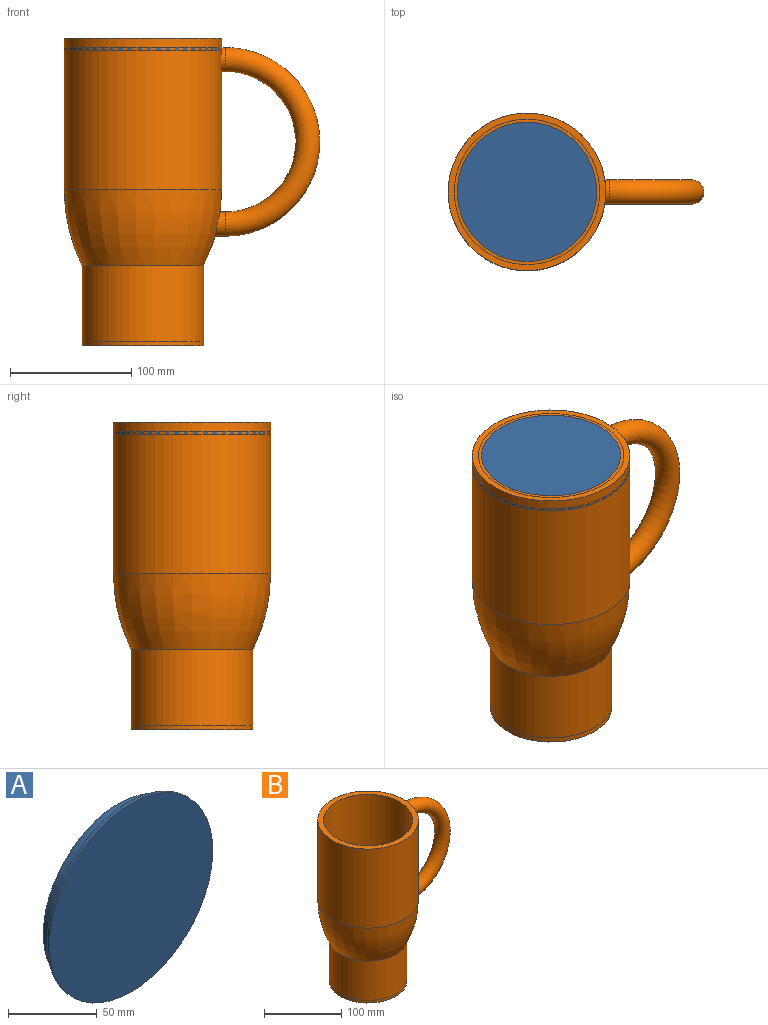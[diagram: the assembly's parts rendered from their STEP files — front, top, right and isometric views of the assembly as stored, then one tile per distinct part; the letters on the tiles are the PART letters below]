
ASSEMBLY  parts=2 mates=1
PART A: 5 faces, bbox 130x10x130 mm
  f0: cylinder r=60mm len=120mm, axis (0,-1,0), area 3015.9mm2, adj f1,f3
  f1: plane 120x120mm, normal (0,1,0), area 11309.7mm2, adj f0
  f2: cylinder r=65mm len=130mm, axis (0,-1,0), area 816.8mm2, adj f3,f4
  f3: plane 130x130mm, normal (0,1,0), area 1963.5mm2, adj f0,f2
  f4: plane 130x130mm, normal (0,-1,0), area 13273.2mm2, adj f2
PART B: 12 faces, bbox 217.3x130x254 mm
  f0: plane 100.36x100.36mm, normal (0,0,-1), area 7910.9mm2, adj f1
  f1: cylinder r=50.18mm len=100.36mm, axis (0,0,-1), area 20908.1mm2, adj f0,f2
  f2: revolved ~130x130mm, area 24191.2mm2, adj f1,f3,f5
  f3: cylinder r=65mm len=130mm, axis (0,0,-1), area 50737.8mm2, adj f2,f4,f6
  f4: plane 130x130mm, normal (0,0,1), area 2886.3mm2, adj f3,f8
  f5: cylinder r=10mm len=20mm, axis (1,0,0), area 415mm2, adj f2,f7
  f6: cylinder r=10mm len=20mm, axis (-1,0,0), area 218.3mm2, adj f3,f7
  f7: torus R=67.79mm, axis (0,-1,0), area 13381.4mm2, adj f5,f6
  f8: cylinder r=57.5mm len=125.5mm, axis (0,0,1), area 45341mm2, adj f4,f11
  f9: plane 100x100mm, normal (0,0,1), area 7854mm2, adj f10
  f10: cylinder r=50mm len=117mm, axis (0,0,1), area 36756.6mm2, adj f9,f11
  f11: cone r=58mm half-angle=45deg, axis (0,0,1), area 3582.1mm2, adj f8,f10
PLACE A rot(axis=(1,0,0),90deg) t=(37.28,52.14,127.91)mm
PLACE B t=(37.28,52.14,-49.78)mm
MATE fastened A.f0 <-> B.f8  axis (0,0,1) through (37.28,52.14,137.91)mm
